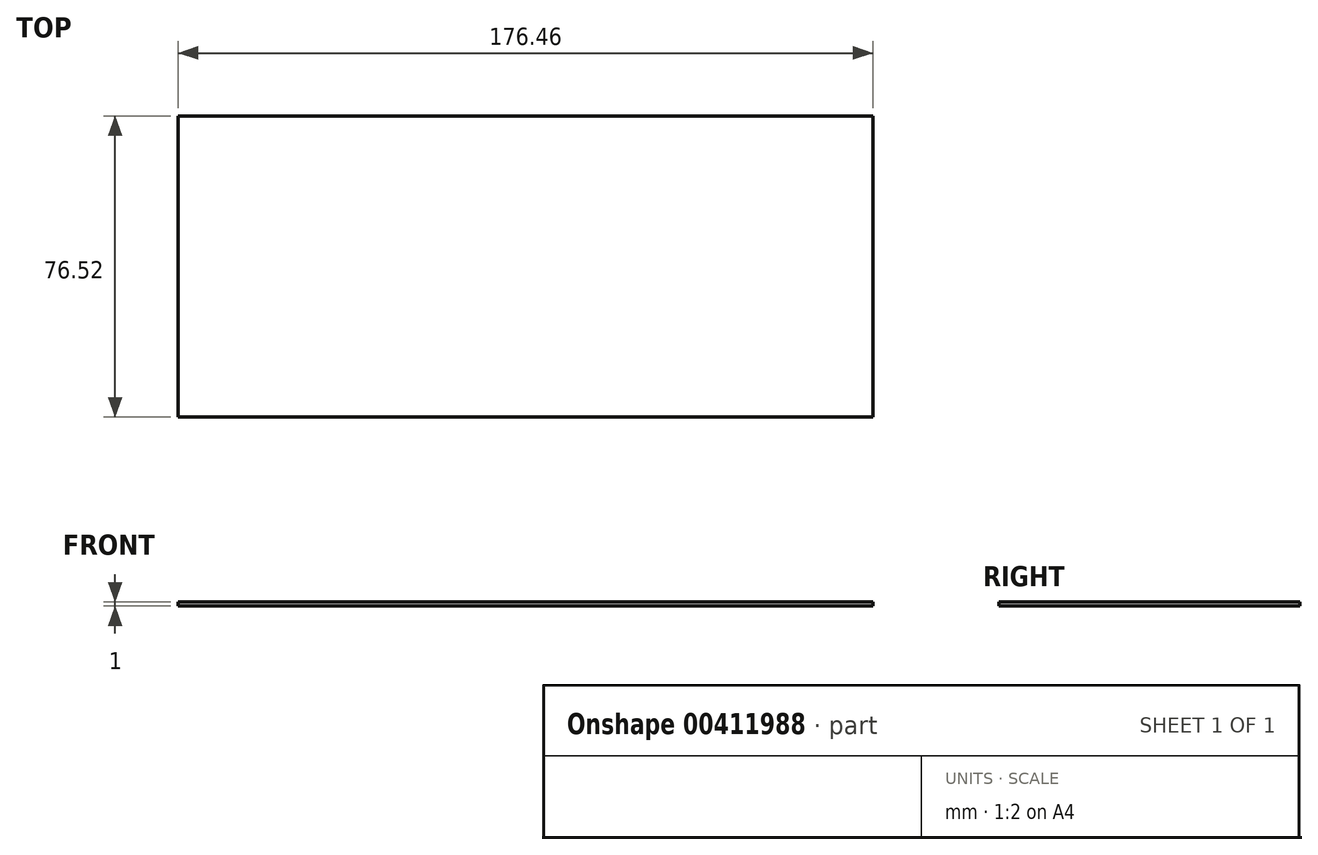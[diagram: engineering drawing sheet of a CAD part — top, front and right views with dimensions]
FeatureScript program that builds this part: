
annotation { "Feature Type Name" : "Feature", "Feature Type Description" : "" }
export const myFeature = defineFeature(function(context is Context, id is Id, definition is map)
    precondition{}
    {
        {
            var Q0;
            Q0=qCreatedBy(makeId("Top.planeOp"),FACE);
            var sketch = newSketch(context, id + "F0", { "sketchPlane" : qUnion([Q0])});
            skLineSegment(sketch, "E0.bottom", {"start": v(-88.23, -38.26) * mm, "end": v(88.23, -38.26) * mm});
            skLineSegment(sketch, "E0.top", {"start": v(-88.23, 38.26) * mm, "end": v(88.23, 38.26) * mm});
            skLineSegment(sketch, "E0.left", {"start": v(-88.23, -38.26) * mm, "end": v(-88.23, 38.26) * mm});
            skLineSegment(sketch, "E0.right", {"start": v(88.23, -38.26) * mm, "end": v(88.23, 38.26) * mm});
            skPoint(sketch, "E0.middle", {"position": v(0, 0) * mm});
            skSolve(sketch);
        }
        {
            var Q0;
            Q0 = qSketchRegion(id + "F0", true);
            extrude(context, id + "F1", {"entities" : qUnion([Q0]), "depth" : 1 * mm});
        }
    });
